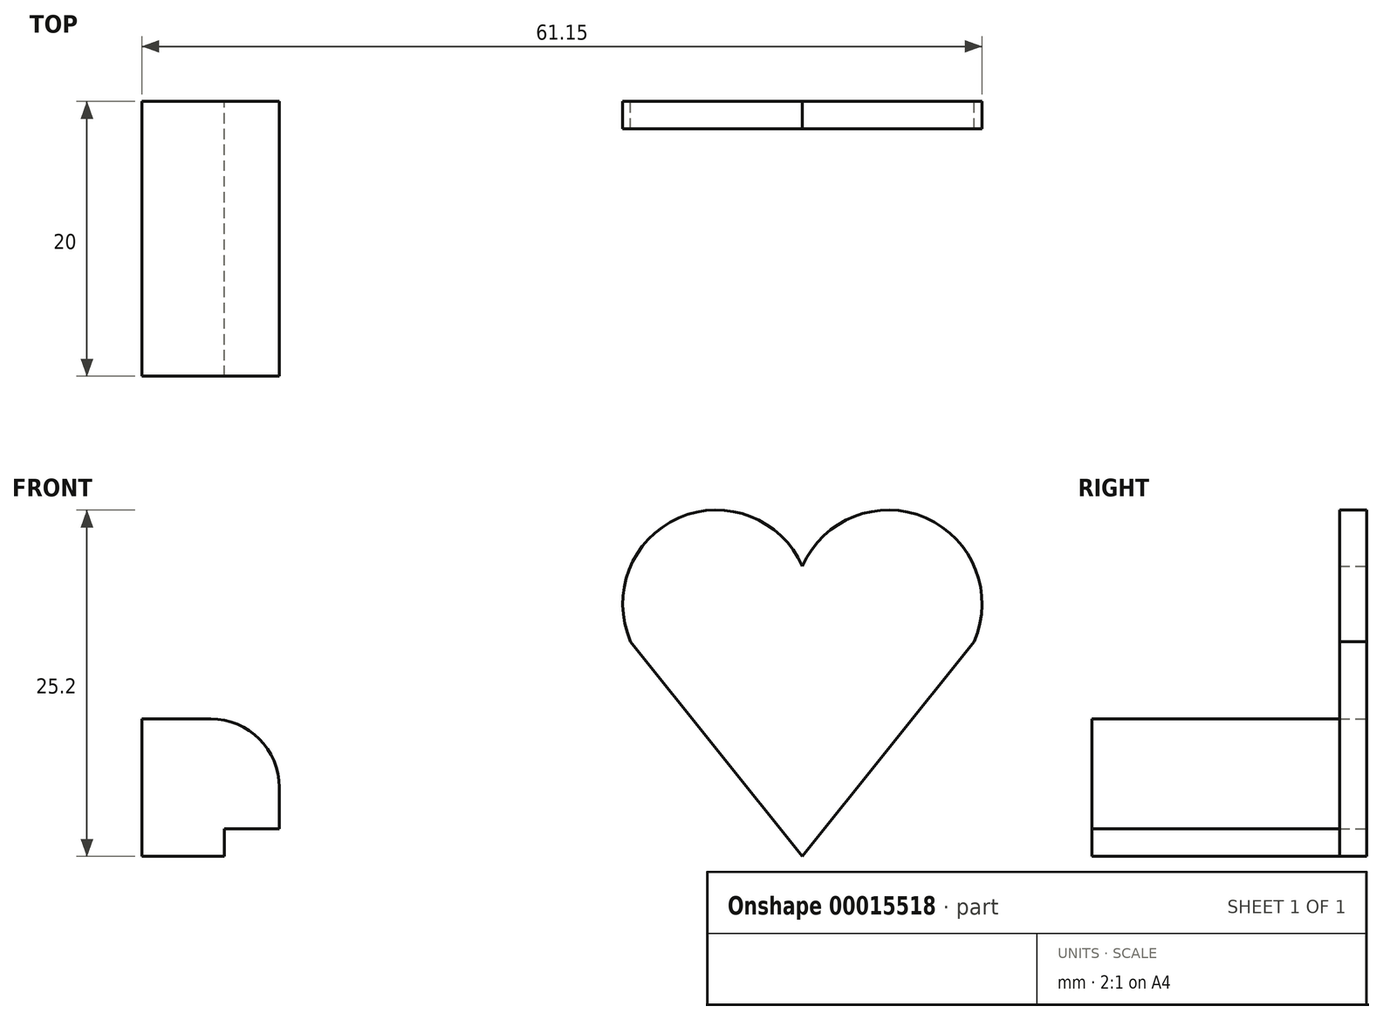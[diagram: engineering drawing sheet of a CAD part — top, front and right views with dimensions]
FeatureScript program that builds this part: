
annotation { "Feature Type Name" : "Feature", "Feature Type Description" : "" }
export const myFeature = defineFeature(function(context is Context, id is Id, definition is map)
    precondition{}
    {
        {
            var Q0;
            Q0=qCreatedBy(makeId("Front.planeOp"),FACE);
            var sketch = newSketch(context, id + "F0", { "sketchPlane" : qUnion([Q0])});
            skLineSegment(sketch, "E0", {"start": v(0, 0) * mm, "end": v(-6, 0) * mm});
            skLineSegment(sketch, "E1", {"start": v(-6, 0) * mm, "end": v(-6, 10) * mm});
            skLineSegment(sketch, "E2", {"start": v(-6, 10) * mm, "end": v(-1, 10) * mm});
            skArc(sketch, "E3", {"start": v(4, 5) * mm, "mid": v(2.54, 8.54) * mm, "end": v(-1, 10) * mm});
            skLineSegment(sketch, "E4", {"start": v(4, 5) * mm, "end": v(4, 2) * mm});
            skLineSegment(sketch, "E5", {"start": v(4, 2) * mm, "end": v(0, 2) * mm});
            skLineSegment(sketch, "E6", {"start": v(0, 2) * mm, "end": v(0, 0) * mm});
            skSolve(sketch);
        }
        {
            var Q0;
            Q0=makeQuery(id+"F0.imprint","IMPRINT",FACE,{"disambiguationData":[TD([[makeQuery(id+"F0.imprint","IMPRINT",EDGE,{"derivedFrom":sQuery(id+"F0.wireOp",EDGE,"E0")}),-1.0]])]});
            extrude(context, id + "F1", {"entities" : qUnion([Q0]), "depth" : 20 * mm});
        }
        {
            var Q0;
            Q0=qCreatedBy(makeId("Front.planeOp"),FACE);
            var sketch = newSketch(context, id + "F2", { "sketchPlane" : qUnion([Q0])});
            skLineSegment(sketch, "E7", {"start": v(42.07, 0) * mm, "end": v(54.57, 15.63) * mm});
            skArc(sketch, "E8", {"start": v(54.57, 15.63) * mm, "mid": v(51.06, 24.62) * mm, "end": v(42.07, 21.12) * mm});
            skLineSegment(sketch, "E9", {"start": v(42.07, 0) * mm, "end": v(42.07, 35.48) * mm, "construction": true});
            skArc(sketch, "E10.MirrorCS", {"start": v(29.57, 15.63) * mm, "mid": v(33.08, 24.62) * mm, "end": v(42.07, 21.12) * mm});
            skLineSegment(sketch, "E11.MirrorCS", {"start": v(42.07, 0) * mm, "end": v(29.57, 15.63) * mm});
            skPoint(sketch, "E12.orphan", {"position": v(42.07, 15.63) * mm});
            skSolve(sketch);
        }
        {
            var Q0;
            Q0=makeQuery(id+"F2.imprint","IMPRINT",FACE,{"disambiguationData":[TD([[makeQuery(id+"F2.imprint","IMPRINT",EDGE,{"derivedFrom":sQuery(id+"F2.wireOp",EDGE,"E7")}),1.0]])]});
            extrude(context, id + "F3", {"entities" : qUnion([Q0]), "depth" : 1.98 * mm});
        }
    });
